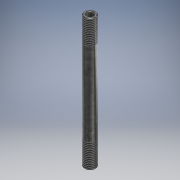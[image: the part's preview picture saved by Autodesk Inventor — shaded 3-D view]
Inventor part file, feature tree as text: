
AUTODESK INVENTOR PART (.ipt)
format: ipt  version: 2017 (Build 210142000, 142)  size: 112,128 bytes
history: native  units: mm
features: thread x2, extrude x1, plane x1, chamfer x1, sketch x1
ambient origin geometry x8: Origin, YZ Plane, XZ Plane, XY Plane, X Axis, Y Axis, Z Axis, Center Point
bodies: Solid1 (feature_tree)
feature tree (6):
  extrude  "Extrusion1"  Depth=108.2mm
  thread  "Thread1"  [1 undecoded]
  plane  "Work Plane1"
  thread  "Thread2"  [1 undecoded]
  chamfer  "Chamfer2"  Distance=20.0mm
  sketch  "Sketch1"  dims[d0=9.0mm d1=5.12mm d2=108.2mm d3=0.0mm d4=20.0mm d5=0.0mm d9=20.0mm d10=0.0mm d11=0.5mm d12=2.0mm d13=45.0deg]
note: 2 required parameter values undecoded (feature->parameter linkage not recoverable at this tier; creation-order binding heuristic only, values carry confidence <= 0.55)
